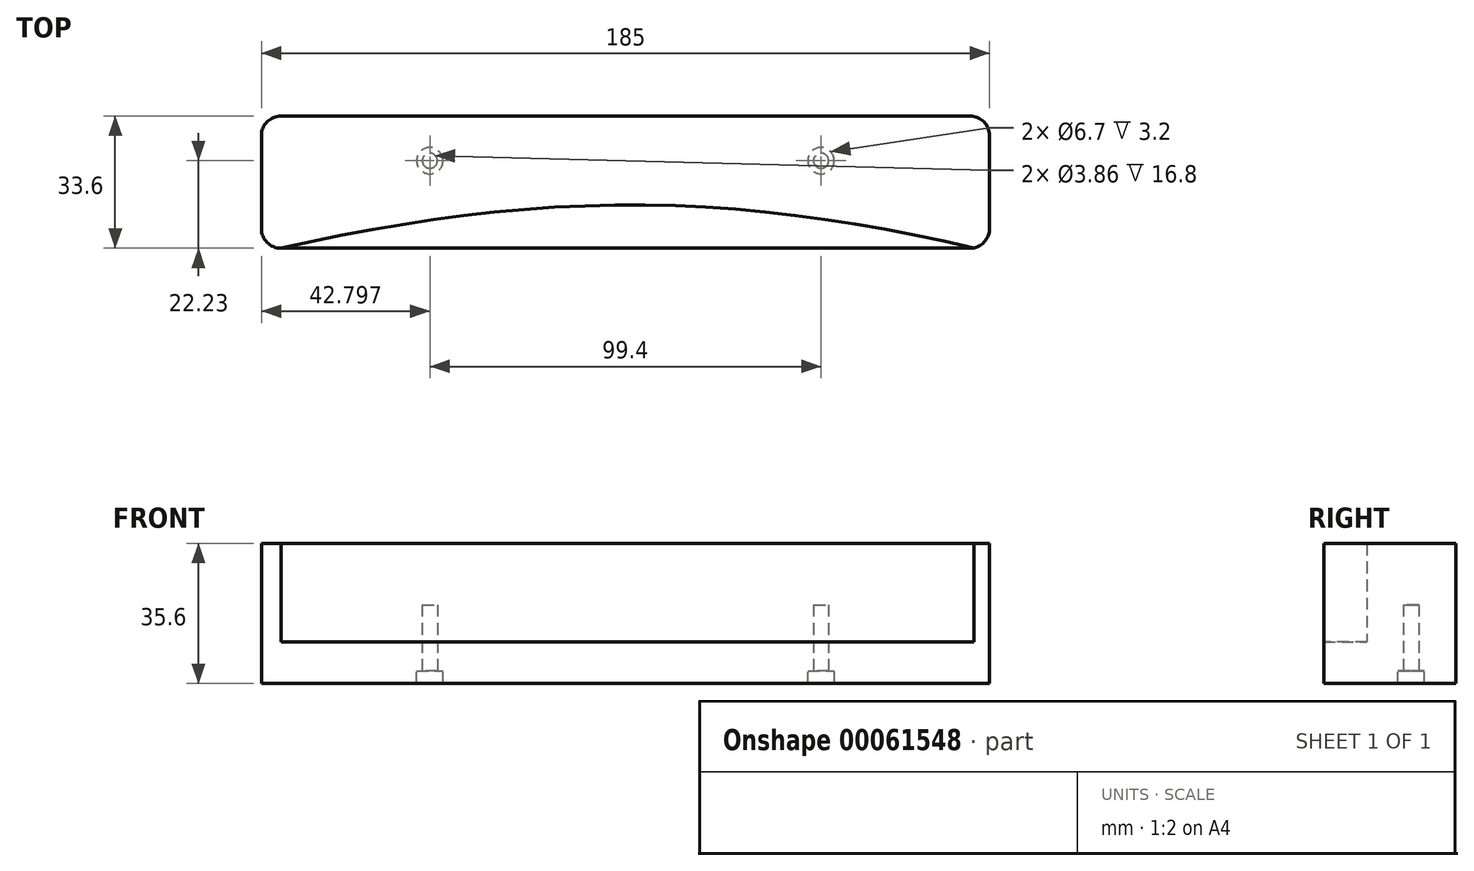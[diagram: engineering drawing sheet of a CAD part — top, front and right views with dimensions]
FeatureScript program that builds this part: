
annotation { "Feature Type Name" : "Feature", "Feature Type Description" : "" }
export const myFeature = defineFeature(function(context is Context, id is Id, definition is map)
    precondition{}
    {
        {
            var Q0;
            Q0=qCreatedBy(makeId("Top.planeOp"),FACE);
            var sketch = newSketch(context, id + "F0", { "sketchPlane" : qUnion([Q0])});
            skLineSegment(sketch, "E0.bottom", {"start": v(-89.36, -7.5) * mm, "end": v(85.64, -7.5) * mm});
            skLineSegment(sketch, "E0.top", {"start": v(-89.36, -41.1) * mm, "end": v(85.64, -41.1) * mm});
            skLineSegment(sketch, "E0.left", {"start": v(-94.36, -12.5) * mm, "end": v(-94.36, -36.1) * mm});
            skLineSegment(sketch, "E0.right", {"start": v(90.64, -12.5) * mm, "end": v(90.64, -36.1) * mm});
            skPoint(sketch, "E1.visualSharp", {"position": v(-94.36, -7.5) * mm});
            skArc(sketch, "E1.filletArc", {"start": v(-89.36, -7.5) * mm, "mid": v(-92.9, -8.97) * mm, "end": v(-94.36, -12.5) * mm});
            skPoint(sketch, "E2.visualSharp", {"position": v(-94.36, -41.1) * mm});
            skArc(sketch, "E2.filletArc", {"start": v(-94.36, -36.1) * mm, "mid": v(-92.9, -39.64) * mm, "end": v(-89.36, -41.1) * mm});
            skPoint(sketch, "E3.visualSharp", {"position": v(90.64, -41.1) * mm});
            skArc(sketch, "E3.filletArc", {"start": v(85.64, -41.1) * mm, "mid": v(89.17, -39.64) * mm, "end": v(90.64, -36.1) * mm});
            skPoint(sketch, "E4.visualSharp", {"position": v(90.64, -7.5) * mm});
            skArc(sketch, "E4.filletArc", {"start": v(90.64, -12.5) * mm, "mid": v(89.17, -8.97) * mm, "end": v(85.64, -7.5) * mm});
            skFitSpline(sketch, "E5", {"points": [v(-89.36, -41.1) * mm, v(0, -28.27) * mm, v(85.64, -41.1) * mm], "startDerivative": vector(177.84, 38.38) * mm, "endDerivative": vector(172.14, -38.64) * mm});
            skSolve(sketch);
        }
        {
            var Q0;
            {var subQ6=sQuery(id+"F0.wireOp",EDGE,"E0.left");Q0=makeQuery(id+"F0.imprint","IMPRINT",FACE,{"disambiguationData":[TD([[makeQuery(id+"F0.imprint","IMPRINT",EDGE,{"derivedFrom":subQ6}),1.0]])]});}
            var Q1;
            {var subQ0=sQuery(id+"F0.wireOp",EDGE,"E2.filletArc");var subQ1=sQuery(id+"F0.wireOp",EDGE,"E0.top");var subQ2=makeQuery(id+"F0.imprint","INTERSECT",VERTEX,{"derivedFrom":[subQ1,subQ0]});Q1=makeQuery(id+"F0.imprint","IMPRINT",FACE,{"disambiguationData":[TD([[makeQuery(id+"F0.imprint","IMPRINT",EDGE,{"disambiguationData":[TD([[subQ2,-1.0]])],"derivedFrom":subQ1}),1.0]])]});}
            var Q2;
            {var subQ5=sQuery(id+"F0.wireOp",EDGE,"DiWK0a0K-p0Ve-xPCM-Xpb8-uTkeJafHcErU");Q2=makeQuery(id+"F0.imprint","IMPRINT",FACE,{"disambiguationData":[TD([[makeQuery(id+"F0.imprint","IMPRINT",EDGE,{"derivedFrom":subQ5}),1.0]])]});}
            var Q3;
            {var subQ0=sQuery(id+"F0.wireOp",EDGE,"XpN96RJf-h1wa-usSg-oxlj-EXDZ94Ahnvhv");var subQ1=sQuery(id+"F0.wireOp",EDGE,"E0.top");var subQ2=makeQuery(id+"F0.imprint","INTERSECT",VERTEX,{"derivedFrom":[subQ1,subQ0]});Q3=makeQuery(id+"F0.imprint","IMPRINT",FACE,{"disambiguationData":[TD([[makeQuery(id+"F0.imprint","IMPRINT",EDGE,{"disambiguationData":[TD([[subQ2,1.0]])],"derivedFrom":subQ1}),1.0]])]});}
            var Q4;
            {var subQ5=sQuery(id+"F0.wireOp",EDGE,"Qj6dQj5D-QQnR-hAFS-0dMR-JZPYQxWabMse");Q4=makeQuery(id+"F0.imprint","IMPRINT",FACE,{"disambiguationData":[TD([[makeQuery(id+"F0.imprint","IMPRINT",EDGE,{"derivedFrom":subQ5}),-1.0]])]});}
            var Q5;
            {var subQ9=sQuery(id+"F0.wireOp",EDGE,"E0.right");Q5=makeQuery(id+"F0.imprint","IMPRINT",FACE,{"disambiguationData":[TD([[makeQuery(id+"F0.imprint","IMPRINT",EDGE,{"derivedFrom":subQ9}),-1.0]])]});}
            var Q6;
            {var subQ0=sQuery(id+"F0.wireOp",EDGE,"E3.filletArc");var subQ1=sQuery(id+"F0.wireOp",EDGE,"E0.top");var subQ2=makeQuery(id+"F0.imprint","INTERSECT",VERTEX,{"derivedFrom":[subQ1,subQ0]});Q6=makeQuery(id+"F0.imprint","IMPRINT",FACE,{"disambiguationData":[TD([[makeQuery(id+"F0.imprint","IMPRINT",EDGE,{"disambiguationData":[TD([[subQ2,1.0]])],"derivedFrom":subQ1}),1.0]])]});}
            var Q7;
            {var subQ0=sQuery(id+"F0.wireOp",EDGE,"8f524986-9a2f-477d-a438-1098895b14b8");var subQ1=sQuery(id+"F0.wireOp",EDGE,"q3M1eQDT-CZSL-Hfhw-1e6b-vYKe8UV4ZBwo");var subQ2=makeQuery(id+"F0.imprint","INTERSECT",VERTEX,{"disambiguationData":[OD(0.0)],"derivedFrom":[subQ1,subQ0]});Q7=makeQuery(id+"F0.imprint","IMPRINT",FACE,{"disambiguationData":[TD([[makeQuery(id+"F0.imprint","IMPRINT",EDGE,{"disambiguationData":[TD([[subQ2,-1.0]])],"derivedFrom":subQ1}),1.0]])]});}
            var Q8;
            {var subQ0=sQuery(id+"F0.wireOp",EDGE,"f629a123-b092-4783-abd5-7fa05e799837");var subQ1=sQuery(id+"F0.wireOp",EDGE,"q3M1eQDT-CZSL-Hfhw-1e6b-vYKe8UV4ZBwo");var subQ2=makeQuery(id+"F0.imprint","INTERSECT",VERTEX,{"disambiguationData":[OD(0.0)],"derivedFrom":[subQ1,subQ0]});Q8=makeQuery(id+"F0.imprint","IMPRINT",FACE,{"disambiguationData":[TD([[makeQuery(id+"F0.imprint","IMPRINT",EDGE,{"disambiguationData":[TD([[subQ2,-1.0]])],"derivedFrom":subQ1}),1.0]])]});}
            var Q9;
            {var subQ0=sQuery(id+"F0.wireOp",EDGE,"f629a123-b092-4783-abd5-7fa05e799837");var subQ1=sQuery(id+"F0.wireOp",EDGE,"q3M1eQDT-CZSL-Hfhw-1e6b-vYKe8UV4ZBwo");var subQ2=makeQuery(id+"F0.imprint","INTERSECT",VERTEX,{"disambiguationData":[OD(0.0)],"derivedFrom":[subQ1,subQ0]});Q9=makeQuery(id+"F0.imprint","IMPRINT",FACE,{"disambiguationData":[TD([[makeQuery(id+"F0.imprint","IMPRINT",EDGE,{"disambiguationData":[TD([[subQ2,-1.0]])],"derivedFrom":subQ1}),-1.0]])]});}
            var Q10;
            {var subQ0=sQuery(id+"F0.wireOp",EDGE,"8f524986-9a2f-477d-a438-1098895b14b8");var subQ1=sQuery(id+"F0.wireOp",EDGE,"q3M1eQDT-CZSL-Hfhw-1e6b-vYKe8UV4ZBwo");var subQ2=makeQuery(id+"F0.imprint","INTERSECT",VERTEX,{"disambiguationData":[OD(0.0)],"derivedFrom":[subQ1,subQ0]});Q10=makeQuery(id+"F0.imprint","IMPRINT",FACE,{"disambiguationData":[TD([[makeQuery(id+"F0.imprint","IMPRINT",EDGE,{"disambiguationData":[TD([[subQ2,-1.0]])],"derivedFrom":subQ1}),-1.0]])]});}
            var Q11;
            {var subQ0=sQuery(id+"F0.wireOp",EDGE,"e7c36ffa-8dd1-4ad2-a08c-114cf6db0365");var subQ1=sQuery(id+"F0.wireOp",EDGE,"NGp6TUnh-2WYz-SvJ6-BtMD-nmsAgSWZyCNH");var subQ2=makeQuery(id+"F0.imprint","INTERSECT",VERTEX,{"disambiguationData":[OD(0.0)],"derivedFrom":[subQ1,subQ0]});Q11=makeQuery(id+"F0.imprint","IMPRINT",FACE,{"disambiguationData":[TD([[makeQuery(id+"F0.imprint","IMPRINT",EDGE,{"disambiguationData":[TD([[subQ2,-1.0]])],"derivedFrom":subQ1}),1.0]])]});}
            var Q12;
            {var subQ0=sQuery(id+"F0.wireOp",EDGE,"e7c36ffa-8dd1-4ad2-a08c-114cf6db0365");var subQ1=sQuery(id+"F0.wireOp",EDGE,"NGp6TUnh-2WYz-SvJ6-BtMD-nmsAgSWZyCNH");var subQ2=makeQuery(id+"F0.imprint","INTERSECT",VERTEX,{"disambiguationData":[OD(0.0)],"derivedFrom":[subQ1,subQ0]});Q12=makeQuery(id+"F0.imprint","IMPRINT",FACE,{"disambiguationData":[TD([[makeQuery(id+"F0.imprint","IMPRINT",EDGE,{"disambiguationData":[TD([[subQ2,-1.0]])],"derivedFrom":subQ1}),-1.0]])]});}
            var Q13;
            {var subQ0=sQuery(id+"F0.wireOp",EDGE,"635bec6d-890f-4d85-b6bb-3d27c9027523");var subQ1=sQuery(id+"F0.wireOp",EDGE,"NGp6TUnh-2WYz-SvJ6-BtMD-nmsAgSWZyCNH");var subQ2=makeQuery(id+"F0.imprint","INTERSECT",VERTEX,{"disambiguationData":[OD(0.0)],"derivedFrom":[subQ1,subQ0]});Q13=makeQuery(id+"F0.imprint","IMPRINT",FACE,{"disambiguationData":[TD([[makeQuery(id+"F0.imprint","IMPRINT",EDGE,{"disambiguationData":[TD([[subQ2,-1.0]])],"derivedFrom":subQ1}),-1.0]])]});}
            var Q14;
            {var subQ0=sQuery(id+"F0.wireOp",EDGE,"635bec6d-890f-4d85-b6bb-3d27c9027523");var subQ1=sQuery(id+"F0.wireOp",EDGE,"NGp6TUnh-2WYz-SvJ6-BtMD-nmsAgSWZyCNH");var subQ2=makeQuery(id+"F0.imprint","INTERSECT",VERTEX,{"disambiguationData":[OD(0.0)],"derivedFrom":[subQ1,subQ0]});Q14=makeQuery(id+"F0.imprint","IMPRINT",FACE,{"disambiguationData":[TD([[makeQuery(id+"F0.imprint","IMPRINT",EDGE,{"disambiguationData":[TD([[subQ2,-1.0]])],"derivedFrom":subQ1}),1.0]])]});}
            var Q15;
            {var subQ0=sQuery(id+"F0.wireOp",EDGE,"XpN96RJf-h1wa-usSg-oxlj-EXDZ94Ahnvhv");var subQ1=sQuery(id+"F0.wireOp",EDGE,"E0.top");var subQ2=makeQuery(id+"F0.imprint","INTERSECT",VERTEX,{"derivedFrom":[subQ1,subQ0]});Q15=makeQuery(id+"F0.imprint","IMPRINT",FACE,{"disambiguationData":[TD([[makeQuery(id+"F0.imprint","IMPRINT",EDGE,{"disambiguationData":[TD([[subQ2,-1.0]])],"derivedFrom":subQ1}),1.0]])]});}
            extrude(context, id + "F1", {"entities" : qUnion([Q0, Q1, Q2, Q3, Q4, Q5, Q6, Q7, Q8, Q9, Q10, Q11, Q12, Q13, Q14, Q15]), "depth" : 32.4 * mm});
        }
        {
            var Q0;
            Q0=makeQuery(id+"F1.opExtrude","CAP_FACE",FACE,{"disambiguationData":[OSD([sQuery(id+"F0.wireOp",EDGE,"E0.bottom"),sQuery(id+"F0.wireOp",EDGE,"E0.top"),sQuery(id+"F0.wireOp",EDGE,"E0.left"),sQuery(id+"F0.wireOp",EDGE,"E0.right"),sQuery(id+"F0.wireOp",EDGE,"E1.filletArc"),sQuery(id+"F0.wireOp",EDGE,"E2.filletArc"),sQuery(id+"F0.wireOp",EDGE,"E3.filletArc"),sQuery(id+"F0.wireOp",EDGE,"E4.filletArc")])],"isStart":false});
            var sketch = newSketch(context, id + "F2", { "sketchPlane" : qUnion([Q0])});
            skFitSpline(sketch, "E6", {"points": [v(-89.36, -41.1) * mm, v(0, -30.1) * mm, v(86.66, -41) * mm], "startDerivative": vector(178.08, 40.77) * mm, "endDerivative": vector(173.96, -40.8) * mm});
            skSolve(sketch);
        }
        {
            var Q0;
            {var subQ0=sQuery(id+"F2.wireOp",EDGE,"E6");Q0=makeQuery(id+"F2.imprint","IMPRINT",FACE,{"disambiguationData":[TD([[makeQuery(id+"F2.imprint","IMPRINT",EDGE,{"derivedFrom":subQ0}),-1.0]])]});}
            extrude(context, id + "F3", {"entities" : qUnion([Q0]), "operationType" : NewBodyOperationType.REMOVE, "oppositeDirection" : true, "depth" : 25 * mm});
        }
        {
            var Q0;
            Q0=makeQuery(id+"F1.opExtrude","CAP_FACE",FACE,{"disambiguationData":[OSD([sQuery(id+"F0.wireOp",EDGE,"E0.bottom"),sQuery(id+"F0.wireOp",EDGE,"E0.top"),sQuery(id+"F0.wireOp",EDGE,"E0.left"),sQuery(id+"F0.wireOp",EDGE,"E0.right"),sQuery(id+"F0.wireOp",EDGE,"E1.filletArc"),sQuery(id+"F0.wireOp",EDGE,"E2.filletArc"),sQuery(id+"F0.wireOp",EDGE,"E3.filletArc"),sQuery(id+"F0.wireOp",EDGE,"E4.filletArc")])],"isStart":true});
            var sketch = newSketch(context, id + "F4", { "sketchPlane" : qUnion([Q0])});
            skLineSegment(sketch, "E7", {"start": v(-94.36, 24.3) * mm, "end": v(-94.36, 18.87) * mm});
            skLineSegment(sketch, "E8", {"start": v(-94.36, 18.87) * mm, "end": v(90.64, 18.87) * mm});
            skLineSegment(sketch, "E9", {"start": v(-1.86, 18.87) * mm, "end": v(-51.56, 18.87) * mm});
            skLineSegment(sketch, "E10", {"start": v(-1.86, 18.87) * mm, "end": v(47.84, 18.87) * mm});
            skCircle(sketch, "E11", {"center": v(47.84, 18.87) * mm, "radius": 3.35 * mm});
            skCircle(sketch, "E12", {"center": v(-51.56, 18.87) * mm, "radius": 3.35 * mm});
            skSolve(sketch);
        }
        {
            var Q0;
            {var subQ0=sQuery(id+"F4.wireOp",EDGE,"E9");var subQ1=sQuery(id+"F4.wireOp",EDGE,"E8");var subQ2=makeQuery(id+"F4.imprint","INTERSECT",VERTEX,{"derivedFrom":[subQ1,subQ0]});Q0=makeQuery(id+"F4.imprint","IMPRINT",FACE,{"disambiguationData":[TD([[makeQuery(id+"F4.imprint","IMPRINT",EDGE,{"disambiguationData":[TD([[subQ2,1.0]])],"derivedFrom":subQ1}),-1.0]])]});}
            var Q1;
            {var subQ0=sQuery(id+"F4.wireOp",EDGE,"E9");var subQ1=sQuery(id+"F4.wireOp",EDGE,"E8");var subQ2=makeQuery(id+"F4.imprint","INTERSECT",VERTEX,{"derivedFrom":[subQ1,subQ0]});Q1=makeQuery(id+"F4.imprint","IMPRINT",FACE,{"disambiguationData":[TD([[makeQuery(id+"F4.imprint","IMPRINT",EDGE,{"disambiguationData":[TD([[subQ2,1.0]])],"derivedFrom":subQ1}),1.0]])]});}
            var Q2;
            {var subQ0=sQuery(id+"F4.wireOp",EDGE,"E10");var subQ1=sQuery(id+"F4.wireOp",EDGE,"E8");var subQ2=makeQuery(id+"F4.imprint","INTERSECT",VERTEX,{"derivedFrom":[subQ1,subQ0]});Q2=makeQuery(id+"F4.imprint","IMPRINT",FACE,{"disambiguationData":[TD([[makeQuery(id+"F4.imprint","IMPRINT",EDGE,{"disambiguationData":[TD([[subQ2,-1.0]])],"derivedFrom":subQ1}),1.0]])]});}
            var Q3;
            {var subQ0=sQuery(id+"F4.wireOp",EDGE,"E10");var subQ1=sQuery(id+"F4.wireOp",EDGE,"E8");var subQ2=makeQuery(id+"F4.imprint","INTERSECT",VERTEX,{"derivedFrom":[subQ1,subQ0]});Q3=makeQuery(id+"F4.imprint","IMPRINT",FACE,{"disambiguationData":[TD([[makeQuery(id+"F4.imprint","IMPRINT",EDGE,{"disambiguationData":[TD([[subQ2,-1.0]])],"derivedFrom":subQ1}),-1.0]])]});}
            extrude(context, id + "F5", {"entities" : qUnion([Q0, Q1, Q2, Q3]), "operationType" : NewBodyOperationType.ADD, "depth" : 3.2 * mm});
        }
        {
            var Q0;
            Q0=makeQuery(id+"F5.opExtrude","CAP_FACE",FACE,{"disambiguationData":[OSD([sQuery(id+"F4.wireOp",EDGE,"E11")])],"isStart":false});
            var sketch = newSketch(context, id + "F6", { "sketchPlane" : qUnion([Q0])});
            skLineSegment(sketch, "E13", {"start": v(46.98, 15.63) * mm, "end": v(47.84, 18.87) * mm});
            skLineSegment(sketch, "E14", {"start": v(-53.1, 16.63) * mm, "end": v(-51.56, 18.87) * mm});
            skCircle(sketch, "E15", {"center": v(47.84, 18.87) * mm, "radius": 1.93 * mm});
            skCircle(sketch, "E16", {"center": v(-51.56, 18.87) * mm, "radius": 1.93 * mm});
            skSolve(sketch);
        }
        {
            var Q0;
            Q0=makeQuery(id+"F6.imprint","IMPRINT",FACE,{"disambiguationData":[TD([[makeQuery(id+"F6.imprint","IMPRINT",EDGE,{"derivedFrom":sQuery(id+"F6.wireOp",EDGE,"E15")}),1.0]])]});
            var Q1;
            Q1=makeQuery(id+"F6.imprint","IMPRINT",FACE,{"disambiguationData":[TD([[makeQuery(id+"F6.imprint","IMPRINT",EDGE,{"derivedFrom":sQuery(id+"F6.wireOp",EDGE,"E16")}),1.0]])]});
            extrude(context, id + "F7", {"entities" : qUnion([Q0, Q1]), "operationType" : NewBodyOperationType.REMOVE, "oppositeDirection" : true, "depth" : 20 * mm});
        }
    });
